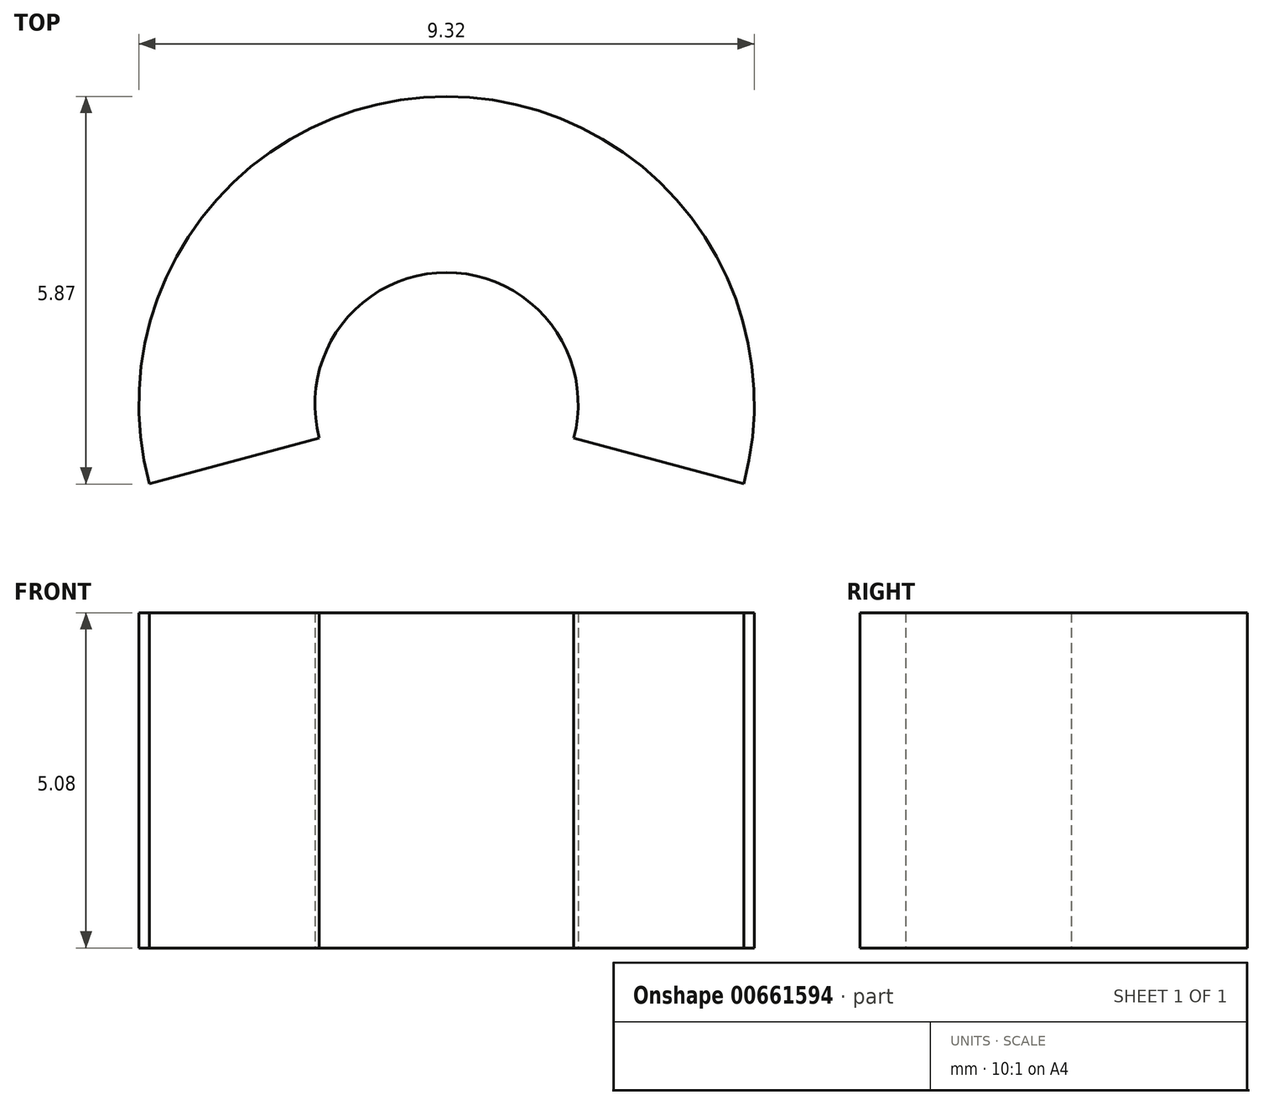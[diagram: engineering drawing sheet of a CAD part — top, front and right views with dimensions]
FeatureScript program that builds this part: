
annotation { "Feature Type Name" : "Feature", "Feature Type Description" : "" }
export const myFeature = defineFeature(function(context is Context, id is Id, definition is map)
    precondition{}
    {
        {
            var Q0;
            Q0=qCreatedBy(makeId("Top.planeOp"),FACE);
            var sketch = newSketch(context, id + "F0", { "sketchPlane" : qUnion([Q0])});
            skCircle(sketch, "E0", {"center": v(0, 0) * mm, "radius": 4.66 * mm});
            skCircle(sketch, "E1", {"center": v(0, 0) * mm, "radius": 2 * mm});
            skLineSegment(sketch, "E2", {"start": v(-4.5, -1.2) * mm, "end": v(0, 0) * mm});
            skLineSegment(sketch, "E3", {"start": v(0, 0) * mm, "end": v(4.5, -1.2) * mm});
            skLineSegment(sketch, "E4", {"start": v(-4.66, 0) * mm, "end": v(4.66, 0) * mm, "construction": true});
            skSolve(sketch);
        }
        {
            var Q0;
            {var subQ0=sQuery(id+"F0.wireOp",EDGE,"E2");var subQ1=sQuery(id+"F0.wireOp",EDGE,"E0");var subQ2=makeQuery(id+"F0.imprint","INTERSECT",VERTEX,{"derivedFrom":[subQ1,subQ0]});Q0=makeQuery(id+"F0.imprint","IMPRINT",FACE,{"disambiguationData":[TD([[makeQuery(id+"F0.imprint","IMPRINT",EDGE,{"disambiguationData":[TD([[subQ2,1.0]])],"derivedFrom":subQ1}),1.0]])]});}
            extrude(context, id + "F1", {"entities" : qUnion([Q0]), "depth" : 5.08 * mm, "offsetDistance" : 25.4 * mm});
        }
    });
